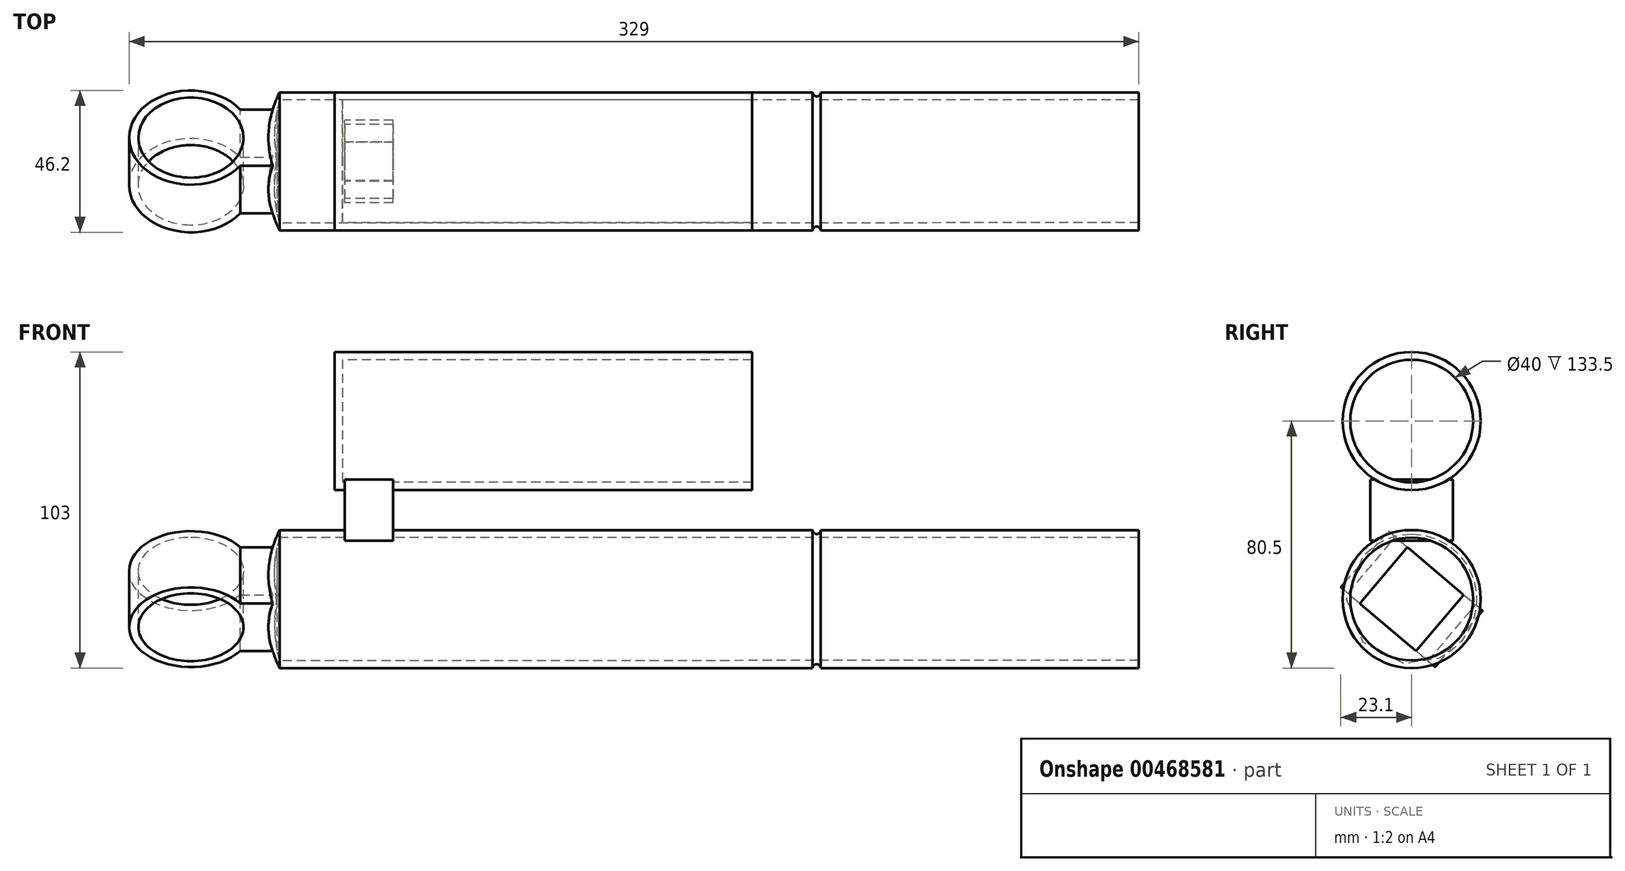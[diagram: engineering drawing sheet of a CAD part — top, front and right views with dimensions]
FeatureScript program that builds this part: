
annotation { "Feature Type Name" : "Feature", "Feature Type Description" : "" }
export const myFeature = defineFeature(function(context is Context, id is Id, definition is map)
    precondition{}
    {
        {
            var Q0;
            Q0=qCreatedBy(makeId("Front.planeOp"),FACE);
            var sketch = newSketch(context, id + "F0", { "sketchPlane" : qUnion([Q0])});
            skCircle(sketch, "E0", {"center": v(0, 0) * mm, "radius": 20.1 * mm, "construction": true});
            skPoint(sketch, "E1", {"position": v(308.9, 0) * mm});
            skLineSegment(sketch, "E2", {"start": v(308.9, 0) * mm, "end": v(308.9, 22.5) * mm});
            skLineSegment(sketch, "E3", {"start": v(308.9, 22.5) * mm, "end": v(205.2, 22.5) * mm});
            skLineSegment(sketch, "E4", {"start": v(28.9, 22.5) * mm, "end": v(28.9, 0) * mm});
            skLineSegment(sketch, "E5", {"start": v(28.9, 0) * mm, "end": v(308.9, 0) * mm, "construction": true});
            skPoint(sketch, "E6", {"position": v(308.9, 20) * mm});
            skLineSegment(sketch, "E7", {"start": v(308.9, 20) * mm, "end": v(28.9, 20.1) * mm});
            skPoint(sketch, "E7.endSnap0", {"position": v(28.9, 11.25) * mm});
            skPoint(sketch, "E8", {"position": v(23.9, 0) * mm});
            skPoint(sketch, "E9", {"position": v(28.9, -22.5) * mm});
            skPoint(sketch, "E10", {"position": v(28.9, -20) * mm});
            skArc(sketch, "E11", {"start": v(28.9, 22.5) * mm, "mid": v(25.17, 11.52) * mm, "end": v(23.9, 0) * mm});
            skArc(sketch, "E12", {"start": v(28.9, 20.1) * mm, "mid": v(27.02, 10.12) * mm, "end": v(26.4, 0) * mm});
            skLineSegment(sketch, "E13", {"start": v(23.9, 0) * mm, "end": v(26.4, 0) * mm});
            skPoint(sketch, "E14", {"position": v(203.9, 22.5) * mm});
            skArc(sketch, "E15", {"start": v(202.6, 22.5) * mm, "mid": v(203.9, 21.2) * mm, "end": v(205.2, 22.5) * mm});
            skLineSegment(sketch, "E16.trimOffspring", {"start": v(202.6, 22.5) * mm, "end": v(28.9, 22.5) * mm});
            skSolve(sketch);
        }
        {
            var Q0;
            Q0 = qSketchRegion(id + "F0", true);
            var Q1;
            Q1=sQuery(id+"F0.wireOp",EDGE,"E5");
            revolve(context, id + "F1", {"entities" : qUnion([Q0]), "axis" : qUnion([Q1]), "revolveType" : RevolveType.FULL});
        }
        {
            var Q0;
            Q0=qCreatedBy(makeId("Front.planeOp"),FACE);
            var sketch = newSketch(context, id + "F2", { "sketchPlane" : qUnion([Q0])});
            skPoint(sketch, "E17", {"position": v(182.9, 58) * mm});
            skLineSegment(sketch, "E18", {"start": v(182.9, 58) * mm, "end": v(182.9, 80.5) * mm});
            skLineSegment(sketch, "E19", {"start": v(182.9, 80.5) * mm, "end": v(46.9, 80.5) * mm});
            skLineSegment(sketch, "E20", {"start": v(46.9, 80.5) * mm, "end": v(46.9, 58) * mm});
            skLineSegment(sketch, "E21", {"start": v(46.9, 58) * mm, "end": v(182.9, 58) * mm, "construction": true});
            skPoint(sketch, "E22", {"position": v(182.9, 78) * mm});
            skLineSegment(sketch, "E23", {"start": v(182.9, 78) * mm, "end": v(49.4, 78) * mm});
            skLineSegment(sketch, "E24", {"start": v(49.4, 78) * mm, "end": v(49.4, 58) * mm});
            skLineSegment(sketch, "E25", {"start": v(49.4, 58) * mm, "end": v(46.9, 58) * mm});
            skSolve(sketch);
        }
        {
            var Q0;
            Q0 = qSketchRegion(id + "F2", true);
            var Q1;
            Q1=sQuery(id+"F2.wireOp",EDGE,"E21");
            revolve(context, id + "F3", {"entities" : qUnion([Q0]), "axis" : qUnion([Q1]), "revolveType" : RevolveType.FULL});
        }
        {
            var Q0;
            Q0=qCreatedBy(makeId("Front.planeOp"),FACE);
            var sketch = newSketch(context, id + "F4", { "sketchPlane" : qUnion([Q0])});
            skPoint(sketch, "E26", {"position": v(58, 29) * mm});
            skLineSegment(sketch, "E27.bottom", {"start": v(65.9, 39) * mm, "end": v(50.1, 39) * mm});
            skLineSegment(sketch, "E27.top", {"start": v(65.9, 19) * mm, "end": v(50.1, 19) * mm});
            skLineSegment(sketch, "E27.left", {"start": v(65.9, 39) * mm, "end": v(65.9, 19) * mm});
            skLineSegment(sketch, "E27.right", {"start": v(50.1, 39) * mm, "end": v(50.1, 19) * mm});
            skSolve(sketch);
        }
        {
            var Q0;
            Q0 = qSketchRegion(id + "F4", true);
            extrude(context, id + "F5", {"entities" : qUnion([Q0]), "operationType" : NewBodyOperationType.ADD, "depth" : 27 * mm, "offsetDistance" : 25 * mm, "symmetric" : true});
        }
        {
            var Q0;
            Q0=qCreatedBy(makeId("Right.planeOp"),FACE);
            var sketch = newSketch(context, id + "F6", { "sketchPlane" : qUnion([Q0])});
            skLineSegment(sketch, "E28", {"start": v(-23.1, 3.82) * mm, "end": v(-7.6, 22.14) * mm});
            skLineSegment(sketch, "E29", {"start": v(-7.6, 22.14) * mm, "end": v(23.1, -3.82) * mm});
            skLineSegment(sketch, "E30", {"start": v(23.1, -3.82) * mm, "end": v(7.6, -22.14) * mm});
            skLineSegment(sketch, "E31", {"start": v(7.6, -22.14) * mm, "end": v(-23.1, 3.82) * mm});
            skPoint(sketch, "E32", {"position": v(7.75, 9.16) * mm});
            skPoint(sketch, "E33", {"position": v(-7.75, -9.16) * mm});
            skLineSegment(sketch, "E34", {"start": v(7.75, 9.16) * mm, "end": v(-7.75, -9.16) * mm, "construction": true});
            skPoint(sketch, "E35", {"position": v(15.35, -12.98) * mm});
            skPoint(sketch, "E36", {"position": v(-15.35, 12.98) * mm});
            skLineSegment(sketch, "E37", {"start": v(15.35, -12.98) * mm, "end": v(-15.35, 12.98) * mm, "construction": true});
            skPoint(sketch, "E38", {"position": v(0, 0) * mm});
            skLineSegment(sketch, "E39", {"start": v(0, 0) * mm, "end": v(-30, 0) * mm, "construction": true});
            skSolve(sketch);
        }
        {
            var Q0;
            Q0 = qSketchRegion(id + "F6", true);
            extrude(context, id + "F7", {"entities" : qUnion([Q0]), "depth" : 40.2 * mm, "offsetDistance" : 25 * mm, "symmetric" : true});
        }
        {
            var Q0;
            Q0=makeQuery(id+"F7.opExtrude","SWEPT_FACE",FACE,{"disambiguationData":[OSD([sQuery(id+"F6.wireOp",EDGE,"E29")])]});
            var sketch = newSketch(context, id + "F8", { "sketchPlane" : qUnion([Q0])});
            skCircle(sketch, "E40", {"center": v(0, 0) * mm, "radius": 20.1 * mm});
            skCircle(sketch, "E41", {"center": v(0, 0) * mm, "radius": 17.1 * mm});
            skLineSegment(sketch, "E42.0", {"start": v(20.1, 20.1) * mm, "end": v(-20.1, 20.1) * mm});
            skLineSegment(sketch, "E43.0", {"start": v(20.1, -20.1) * mm, "end": v(20.1, 20.1) * mm});
            skLineSegment(sketch, "E44.0", {"start": v(-20.1, -20.1) * mm, "end": v(-20.1, 20.1) * mm});
            skLineSegment(sketch, "E45.0", {"start": v(20.1, -20.1) * mm, "end": v(-20.1, -20.1) * mm});
            skSolve(sketch);
        }
        {
            var Q0;
            {var subQ0=sQuery(id+"F8.wireOp",EDGE,"E42.0");var subQ1=sQuery(id+"F8.wireOp",EDGE,"E40");var subQ2=makeQuery(id+"F8.imprint","INTERSECT",VERTEX,{"derivedFrom":[subQ1,subQ0]});Q0=makeQuery(id+"F8.imprint","IMPRINT",FACE,{"disambiguationData":[TD([[makeQuery(id+"F8.imprint","IMPRINT",EDGE,{"disambiguationData":[TD([[subQ2,1.0]])],"derivedFrom":subQ1}),-1.0]])]});}
            var Q1;
            {var subQ0=sQuery(id+"F8.wireOp",EDGE,"E42.0");var subQ1=sQuery(id+"F8.wireOp",EDGE,"E40");var subQ2=makeQuery(id+"F8.imprint","INTERSECT",VERTEX,{"derivedFrom":[subQ1,subQ0]});Q1=makeQuery(id+"F8.imprint","IMPRINT",FACE,{"disambiguationData":[TD([[makeQuery(id+"F8.imprint","IMPRINT",EDGE,{"disambiguationData":[TD([[subQ2,-1.0]])],"derivedFrom":subQ1}),-1.0]])]});}
            var Q2;
            {var subQ0=sQuery(id+"F8.wireOp",EDGE,"E44.0");var subQ1=sQuery(id+"F8.wireOp",EDGE,"E40");var subQ2=makeQuery(id+"F8.imprint","INTERSECT",VERTEX,{"derivedFrom":[subQ1,subQ0]});Q2=makeQuery(id+"F8.imprint","IMPRINT",FACE,{"disambiguationData":[TD([[makeQuery(id+"F8.imprint","IMPRINT",EDGE,{"disambiguationData":[TD([[subQ2,-1.0]])],"derivedFrom":subQ1}),-1.0]])]});}
            var Q3;
            {var subQ0=sQuery(id+"F8.wireOp",EDGE,"E43.0");var subQ1=sQuery(id+"F8.wireOp",EDGE,"E40");var subQ2=makeQuery(id+"F8.imprint","INTERSECT",VERTEX,{"derivedFrom":[subQ1,subQ0]});Q3=makeQuery(id+"F8.imprint","IMPRINT",FACE,{"disambiguationData":[TD([[makeQuery(id+"F8.imprint","IMPRINT",EDGE,{"disambiguationData":[TD([[subQ2,1.0]])],"derivedFrom":subQ1}),-1.0]])]});}
            var Q4;
            Q4=makeQuery(id+"F8.imprint","IMPRINT",FACE,{"disambiguationData":[TD([[makeQuery(id+"F8.imprint","IMPRINT",EDGE,{"derivedFrom":sQuery(id+"F8.wireOp",EDGE,"E41")}),1.0]])]});
            extrude(context, id + "F9", {"entities" : qUnion([Q0, Q1, Q2, Q3, Q4]), "operationType" : NewBodyOperationType.REMOVE, "oppositeDirection" : true, "depth" : 25 * mm, "offsetDistance" : 25 * mm});
        }
        {
            var Q0;
            Q0=makeQuery(id+"F7.opExtrude","SWEPT_FACE",FACE,{"disambiguationData":[OSD([sQuery(id+"F6.wireOp",EDGE,"E29")])]});
            var sketch = newSketch(context, id + "F10", { "sketchPlane" : qUnion([Q0])});
            skCircle(sketch, "E46.0", {"center": v(0, 0) * mm, "radius": 20.1 * mm, "construction": true});
            skPoint(sketch, "E47", {"position": v(16.12, 12) * mm});
            skPoint(sketch, "E48", {"position": v(16.12, -12) * mm});
            skLineSegment(sketch, "E49", {"start": v(16.12, 12) * mm, "end": v(28.12, 12) * mm});
            skLineSegment(sketch, "E50", {"start": v(28.12, 12) * mm, "end": v(28.12, -12) * mm});
            skLineSegment(sketch, "E51", {"start": v(28.12, -12) * mm, "end": v(16.12, -12) * mm});
            skSolve(sketch);
        }
        {
            var Q0;
            {var subQ0=sQuery(id+"F10.wireOp",EDGE,"E49");Q0=makeQuery(id+"F10.imprint","IMPRINT",FACE,{"disambiguationData":[TD([[makeQuery(id+"F10.imprint","IMPRINT",EDGE,{"derivedFrom":subQ0}),-1.0]])]});}
            extrude(context, id + "F11", {"entities" : qUnion([Q0]), "operationType" : NewBodyOperationType.ADD, "oppositeDirection" : true, "depth" : 24 * mm, "offsetDistance" : 25 * mm});
        }
    });
